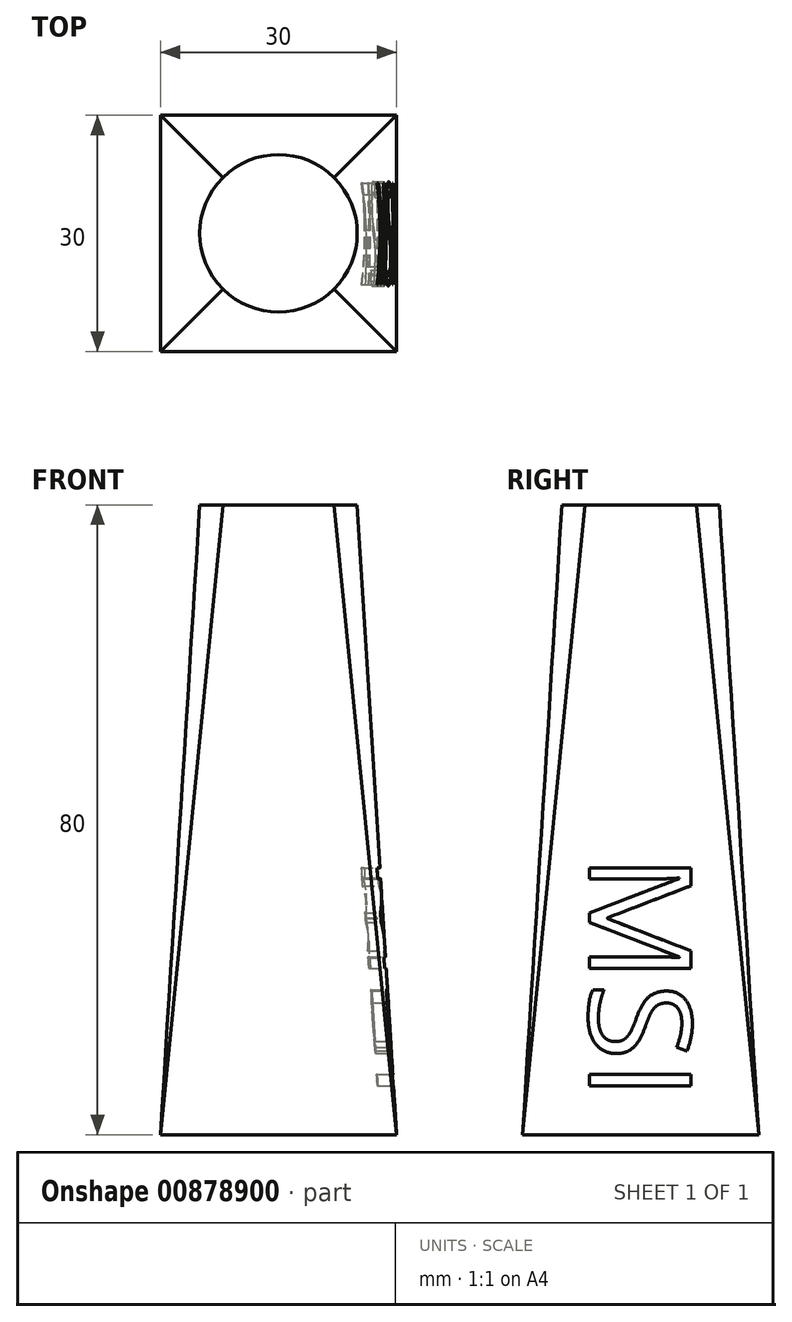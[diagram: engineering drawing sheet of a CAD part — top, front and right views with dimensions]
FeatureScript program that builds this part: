
annotation { "Feature Type Name" : "Feature", "Feature Type Description" : "" }
export const myFeature = defineFeature(function(context is Context, id is Id, definition is map)
    precondition{}
    {
        {
            var Q0;
            Q0=qCreatedBy(makeId("Top.planeOp"),FACE);
            var sketch = newSketch(context, id + "F0", { "sketchPlane" : qUnion([Q0])});
            skLineSegment(sketch, "E0.bottom", {"start": v(15, -15) * mm, "end": v(-15, -15) * mm});
            skLineSegment(sketch, "E0.top", {"start": v(15, 15) * mm, "end": v(-15, 15) * mm});
            skLineSegment(sketch, "E0.left", {"start": v(15, -15) * mm, "end": v(15, 15) * mm});
            skLineSegment(sketch, "E0.right", {"start": v(-15, -15) * mm, "end": v(-15, 15) * mm});
            skPoint(sketch, "E0.middle", {"position": v(0, 0) * mm});
            skSolve(sketch);
        }
        {
            var Q0;
            Q0=qCreatedBy(makeId("Top.planeOp"),FACE);
            cPlane(context, id + "F1", {"entities" : qUnion([Q0]), "cplaneType" : CPlaneType.OFFSET, "offset" : 80 * mm, "width" : 150 * mm, "height" : 150 * mm});
        }
        {
            var Q0;
            Q0=qCreatedBy(id+"F1.planeOp",FACE);
            var sketch = newSketch(context, id + "F2", { "sketchPlane" : qUnion([Q0])});
            skCircle(sketch, "E1", {"center": v(0, 0) * mm, "radius": 10 * mm});
            skSolve(sketch);
        }
        {
            var Q0;
            Q0=makeQuery(id+"F0.imprint","IMPRINT",FACE,{"disambiguationData":[TD([[makeQuery(id+"F0.imprint","IMPRINT",EDGE,{"derivedFrom":sQuery(id+"F0.wireOp",EDGE,"E0.bottom")}),-1.0]])]});
            var Q1;
            Q1=makeQuery(id+"F2.imprint","IMPRINT",FACE,{"disambiguationData":[TD([[makeQuery(id+"F2.imprint","IMPRINT",EDGE,{"derivedFrom":sQuery(id+"F2.wireOp",EDGE,"E1")}),1.0]])]});
            loft(context, id + "F3", {"sheetProfilesArray" : [{ "sheetProfileEntities" : qUnion([Q0]) }, { "sheetProfileEntities" : qUnion([Q1]) }]});
        }
        {
            var Q0;
            Q0=qCreatedBy(makeId("Right.planeOp"),FACE);
            cPlane(context, id + "F4", {"entities" : qUnion([Q0]), "cplaneType" : CPlaneType.OFFSET, "offset" : 50 * mm, "width" : 150 * mm, "height" : 150 * mm});
        }
        {
            var Q0;
            Q0=qCreatedBy(id+"F4.planeOp",FACE);
            var sketch = newSketch(context, id + "F5", { "sketchPlane" : qUnion([Q0])});
            skText(sketch, "E2", { "text": "MSI", "fontName": "OpenSans-Regular.ttf"});
            const initialGuessF5  = {"E2": [-0.0065, 0.03565, 0, -1, 0.013]};
            skSetInitialGuess(sketch, initialGuessF5);
            skSolve(sketch);
        }
        {
            var Q0;
            Q0=qSketchRegion(id+"F5",true);
            var Q1;
            Q1=qConstructionFilter(qBodyType(qCreatedBy(id+"F5",EDGE),BodyType.WIRE),ConstructionObject.NO);
            var Q2;
            Q2=makeQuery(id+"F3.opLoft","SWEPT_FACE",FACE,{"disambiguationData":[OSD([sQuery(id+"F0.wireOp",EDGE,"E0.bottom"),sQuery(id+"F0.wireOp",EDGE,"E0.top"),sQuery(id+"F0.wireOp",EDGE,"E0.left"),sQuery(id+"F2.wireOp",EDGE,"E1")])]});
            var Q3;
            Q3=makeQuery(id+"F3.opLoft","SWEPT_BODY",BODY,{"disambiguationData":[OSD([makeQuery(id+"F0.imprint","IMPRINT",FACE,{"disambiguationData":[TD([[makeQuery(id+"F0.imprint","IMPRINT",EDGE,{"derivedFrom":sQuery(id+"F0.wireOp",EDGE,"E0.bottom")}),-1.0]])]}),makeQuery(id+"F2.imprint","IMPRINT",FACE,{"disambiguationData":[TD([[makeQuery(id+"F2.imprint","IMPRINT",EDGE,{"derivedFrom":sQuery(id+"F2.wireOp",EDGE,"E1")}),1.0]])]})])]});
            extrude(context, id + "F6", {"entities" : qUnion([Q0]), "operationType" : NewBodyOperationType.REMOVE, "surfaceEntities" : qUnion([Q1]), "endBound" : BoundingType.UP_TO_BODY, "oppositeDirection" : true, "depth" : 25 * mm, "endBoundEntityFace" : qUnion([Q2]), "endBoundEntityBody" : qUnion([Q3]), "hasOffset" : true, "offsetDistance" : 2 * mm, "offsetOppositeDirection" : true});
        }
    });
